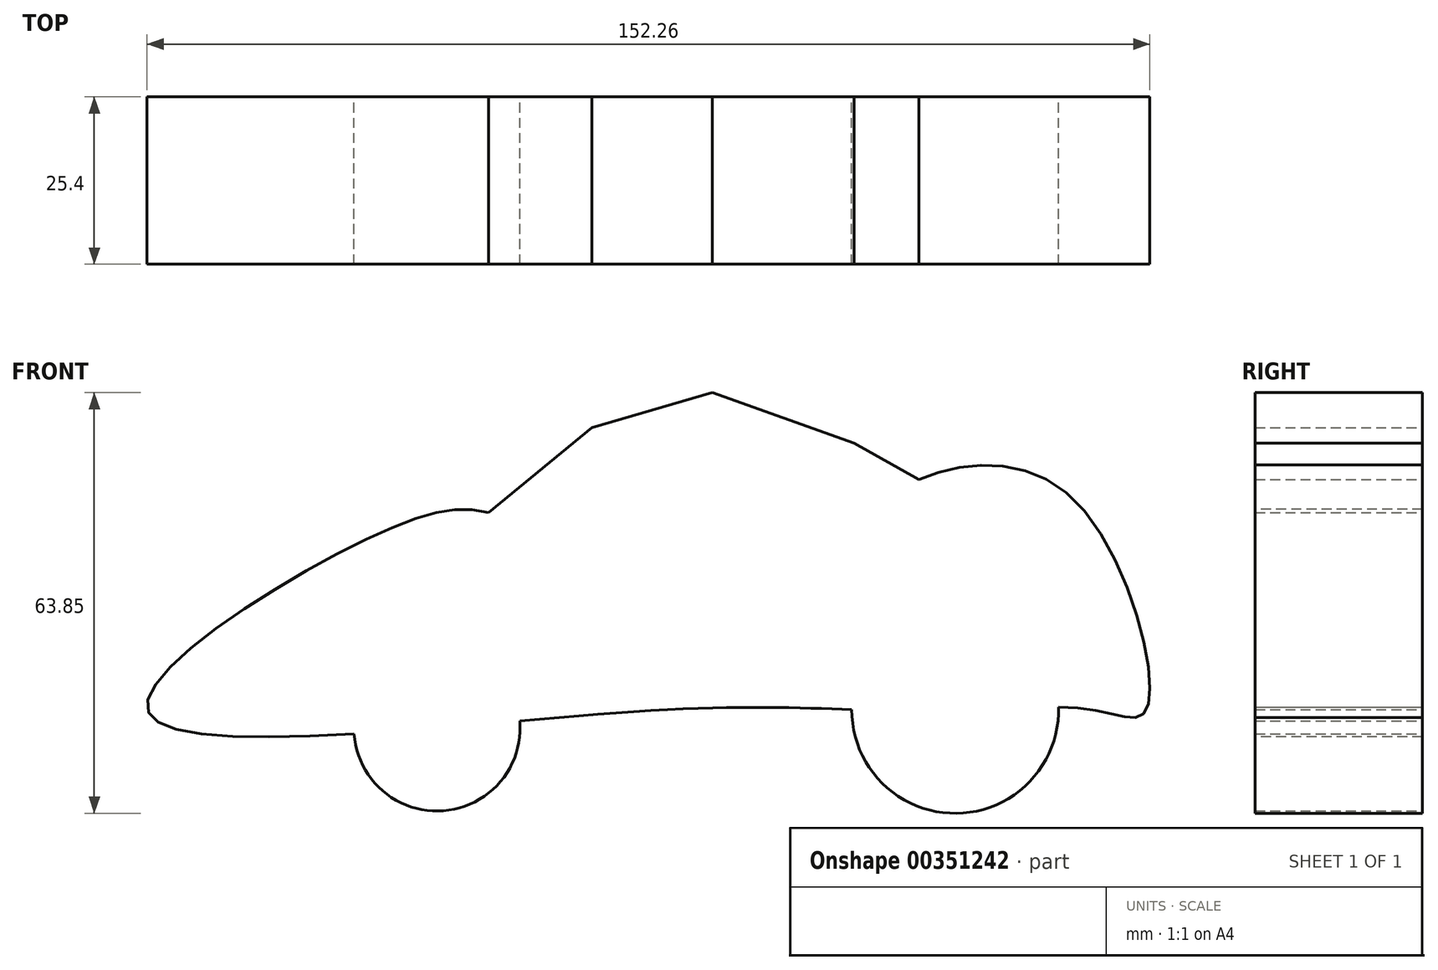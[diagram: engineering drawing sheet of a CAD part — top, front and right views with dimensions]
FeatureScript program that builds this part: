
annotation { "Feature Type Name" : "Feature", "Feature Type Description" : "" }
export const myFeature = defineFeature(function(context is Context, id is Id, definition is map)
    precondition{}
    {
        {
            var Q0;
            Q0=qCreatedBy(makeId("Front.planeOp"),FACE);
            var sketch = newSketch(context, id + "F0", { "sketchPlane" : qUnion([Q0])});
            skFitSpline(sketch, "E0", {"points": [v(-76.07, 0) * mm, v(-40.8, 27) * mm, v(-20.5, 28.58) * mm, v(3.35, 15.37) * mm, v(23.85, 22.07) * mm, v(39.22, 34.3) * mm, v(64.24, 32.32) * mm, v(75.48, 0) * mm, v(68.19, 0) * mm, v(41.98, 0) * mm, v(0, 0) * mm, v(-76.07, 0) * mm]});
            skLineSegment(sketch, "E1", {"start": v(-24.34, 30.07) * mm, "end": v(-8.67, 42.95) * mm});
            skLineSegment(sketch, "E2", {"start": v(-8.67, 42.95) * mm, "end": v(9.66, 48.28) * mm});
            skLineSegment(sketch, "E3", {"start": v(9.66, 48.28) * mm, "end": v(31.14, 40.6) * mm});
            skLineSegment(sketch, "E4", {"start": v(31.14, 40.6) * mm, "end": v(40.99, 35.1) * mm});
            skCircle(sketch, "E5", {"center": v(-32.17, -2.6) * mm, "radius": 12.63 * mm});
            skCircle(sketch, "E6", {"center": v(46.52, 0.13) * mm, "radius": 15.7 * mm});
            skSolve(sketch);
        }
        {
            var Q0;
            {var subQ0=sQuery(id+"F0.wireOp",EDGE,"E1");Q0=makeQuery(id+"F0.imprint","IMPRINT",FACE,{"disambiguationData":[TD([[makeQuery(id+"F0.imprint","IMPRINT",EDGE,{"derivedFrom":subQ0}),-1.0]])]});}
            var Q1;
            {var subQ0=sQuery(id+"F0.wireOp",EDGE,"E5");var subQ1=sQuery(id+"F0.wireOp",EDGE,"E0");var subQ2=makeQuery(id+"F0.imprint","INTERSECT",VERTEX,{"disambiguationData":[OD(0.0)],"derivedFrom":[subQ1,subQ0]});Q1=makeQuery(id+"F0.imprint","IMPRINT",FACE,{"disambiguationData":[TD([[makeQuery(id+"F0.imprint","IMPRINT",EDGE,{"disambiguationData":[TD([[subQ2,-1.0]])],"derivedFrom":subQ1}),-1.0]])]});}
            var Q2;
            {var subQ0=sQuery(id+"F0.wireOp",EDGE,"E5");var subQ1=sQuery(id+"F0.wireOp",EDGE,"E0");var subQ2=makeQuery(id+"F0.imprint","INTERSECT",VERTEX,{"disambiguationData":[OD(0.0)],"derivedFrom":[subQ1,subQ0]});Q2=makeQuery(id+"F0.imprint","IMPRINT",FACE,{"disambiguationData":[TD([[makeQuery(id+"F0.imprint","IMPRINT",EDGE,{"disambiguationData":[TD([[subQ2,-1.0]])],"derivedFrom":subQ1}),1.0]])]});}
            var Q3;
            {var subQ0=sQuery(id+"F0.wireOp",EDGE,"E6");var subQ1=sQuery(id+"F0.wireOp",EDGE,"E0");var subQ2=makeQuery(id+"F0.imprint","INTERSECT",VERTEX,{"disambiguationData":[OD(0.0)],"derivedFrom":[subQ1,subQ0]});Q3=makeQuery(id+"F0.imprint","IMPRINT",FACE,{"disambiguationData":[TD([[makeQuery(id+"F0.imprint","IMPRINT",EDGE,{"disambiguationData":[TD([[subQ2,-1.0]])],"derivedFrom":subQ1}),1.0]])]});}
            var Q4;
            {var subQ0=sQuery(id+"F0.wireOp",EDGE,"E6");var subQ1=sQuery(id+"F0.wireOp",EDGE,"E0");var subQ2=makeQuery(id+"F0.imprint","INTERSECT",VERTEX,{"disambiguationData":[OD(0.0)],"derivedFrom":[subQ1,subQ0]});Q4=makeQuery(id+"F0.imprint","IMPRINT",FACE,{"disambiguationData":[TD([[makeQuery(id+"F0.imprint","IMPRINT",EDGE,{"disambiguationData":[TD([[subQ2,-1.0]])],"derivedFrom":subQ1}),-1.0]])]});}
            var Q5;
            {var subQ1=sQuery(id+"F0.wireOp",EDGE,"E0");var subQ7=makeQuery(id+"F0.imprint","INTERSECT",VERTEX,{"derivedFrom":[subQ1,sQuery(id+"F0.wireOp",EDGE,"E1")]});Q5=makeQuery(id+"F0.imprint","IMPRINT",FACE,{"disambiguationData":[TD([[makeQuery(id+"F0.imprint","IMPRINT",EDGE,{"disambiguationData":[TD([[subQ7,-1.0]])],"derivedFrom":subQ1}),-1.0]])]});}
            extrude(context, id + "F1", {"entities" : qUnion([Q0, Q1, Q2, Q3, Q4, Q5]), "depth" : 25.4 * mm});
        }
    });
